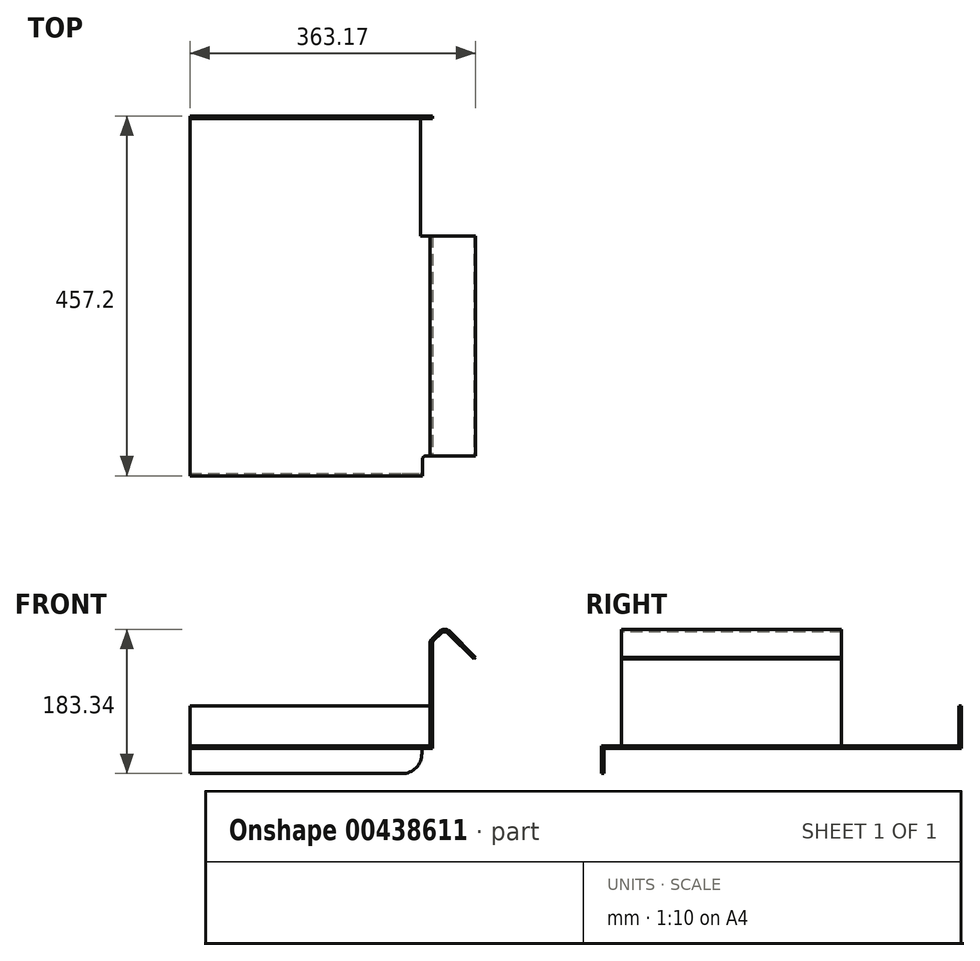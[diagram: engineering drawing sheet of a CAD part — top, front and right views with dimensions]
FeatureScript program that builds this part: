
annotation { "Feature Type Name" : "Feature", "Feature Type Description" : "" }
export const myFeature = defineFeature(function(context is Context, id is Id, definition is map)
    precondition{}
    {
        {
            var Q0;
            Q0=qCreatedBy(makeId("Front.planeOp"),FACE);
            var sketch = newSketch(context, id + "F0", { "sketchPlane" : qUnion([Q0])});
            skCircle(sketch, "E0", {"center": v(0, 0) * mm, "radius": 165.1 * mm});
            skSolve(sketch);
        }
        {
            var Q0;
            Q0=makeQuery(id+"F0.imprint","IMPRINT",FACE,{"disambiguationData":[TD([[makeQuery(id+"F0.imprint","IMPRINT",EDGE,{"derivedFrom":sQuery(id+"F0.wireOp",EDGE,"E0")}),1.0]])]});
            var sketch = newSketch(context, id + "F1", { "sketchPlane" : qUnion([Q0])});
            skLineSegment(sketch, "E1", {"start": v(-76.2, -184.15) * mm, "end": v(76.2, -184.15) * mm});
            skLineSegment(sketch, "E2", {"start": v(0, -184.15) * mm, "end": v(0, 0) * mm});
            skSolve(sketch);
        }
        {
            var Q0;
            Q0=qCreatedBy(makeId("Front.planeOp"),FACE);
            var sketch = newSketch(context, id + "F2", { "sketchPlane" : qUnion([Q0])});
            skLineSegment(sketch, "E3.bottom", {"start": v(-139.7, 0) * mm, "end": v(139.7, 0) * mm});
            skLineSegment(sketch, "E3.top", {"start": v(-139.7, -184.15) * mm, "end": v(139.7, -184.15) * mm});
            skLineSegment(sketch, "E3.left", {"start": v(-139.7, 0) * mm, "end": v(-139.7, -184.15) * mm});
            skLineSegment(sketch, "E3.right", {"start": v(139.7, 0) * mm, "end": v(139.7, -184.15) * mm});
            skLineSegment(sketch, "E4", {"start": v(139.7, -184.15) * mm, "end": v(313.98, -184.15) * mm, "construction": true});
            skSolve(sketch);
        }
        {
            var Q0;
            Q0=qCreatedBy(makeId("Front.planeOp"),FACE);
            var sketch = newSketch(context, id + "F3", { "sketchPlane" : qUnion([Q0])});
            skLineSegment(sketch, "E5", {"start": v(165.1, -184.15) * mm, "end": v(165.1, -54.75) * mm});
            skLineSegment(sketch, "E6", {"start": v(167.89, -48.01) * mm, "end": v(177.22, -38.68) * mm});
            skLineSegment(sketch, "E7", {"start": v(190.7, -38.68) * mm, "end": v(223.47, -71.45) * mm});
            skLineSegment(sketch, "E8", {"start": v(221.23, -73.7) * mm, "end": v(223.47, -71.45) * mm});
            skLineSegment(sketch, "E9", {"start": v(221.23, -73.7) * mm, "end": v(188.45, -40.92) * mm});
            skLineSegment(sketch, "E10", {"start": v(179.47, -40.92) * mm, "end": v(170.13, -50.26) * mm});
            skLineSegment(sketch, "E11", {"start": v(168.28, -54.75) * mm, "end": v(168.28, -184.15) * mm});
            skLineSegment(sketch, "E12", {"start": v(168.28, -184.15) * mm, "end": v(165.1, -184.15) * mm});
            skPoint(sketch, "E13.orphan", {"position": v(167.35, -53.05) * mm});
            skPoint(sketch, "E14.newPointB", {"position": v(168.28, -52.07) * mm});
            skArc(sketch, "E14.filletArc", {"start": v(170.13, -50.26) * mm, "mid": v(168.76, -52.32) * mm, "end": v(168.28, -54.75) * mm});
            skPoint(sketch, "E15.visualSharp", {"position": v(165.1, -50.8) * mm});
            skArc(sketch, "E15.filletArc", {"start": v(167.89, -48.01) * mm, "mid": v(165.83, -51.1) * mm, "end": v(165.1, -54.75) * mm});
            skPoint(sketch, "E16.visualSharp", {"position": v(183.96, -36.43) * mm});
            skArc(sketch, "E16.filletArc", {"start": v(188.45, -40.92) * mm, "mid": v(183.96, -39.06) * mm, "end": v(179.47, -40.92) * mm});
            skPoint(sketch, "E17.visualSharp", {"position": v(183.96, -31.94) * mm});
            skArc(sketch, "E17.filletArc", {"start": v(190.7, -38.68) * mm, "mid": v(183.96, -35.89) * mm, "end": v(177.22, -38.68) * mm});
            skSolve(sketch);
        }
        {
            var Q0;
            Q0=qCreatedBy(makeId("Front.planeOp"),FACE);
            var sketch = newSketch(context, id + "F4", { "sketchPlane" : qUnion([Q0])});
            skLineSegment(sketch, "E18.bottom", {"start": v(-139.7, -184.15) * mm, "end": v(168.28, -184.15) * mm});
            skLineSegment(sketch, "E18.top", {"start": v(-139.7, -187.33) * mm, "end": v(168.28, -187.33) * mm});
            skLineSegment(sketch, "E18.left", {"start": v(-139.7, -184.15) * mm, "end": v(-139.7, -187.33) * mm});
            skLineSegment(sketch, "E18.right", {"start": v(168.28, -184.15) * mm, "end": v(168.28, -187.33) * mm});
            skSolve(sketch);
        }
        {
            var Q0;
            Q0=qCreatedBy(makeId("Front.planeOp"),FACE);
            var sketch = newSketch(context, id + "F5", { "sketchPlane" : qUnion([Q0])});
            skLineSegment(sketch, "E19.bottom", {"start": v(-139.7, -187.33) * mm, "end": v(168.28, -187.33) * mm});
            skLineSegment(sketch, "E19.top", {"start": v(-139.7, -219.23) * mm, "end": v(155.02, -219.23) * mm});
            skLineSegment(sketch, "E19.left", {"start": v(-139.7, -187.33) * mm, "end": v(-139.7, -219.23) * mm});
            skLineSegment(sketch, "E19.right", {"start": v(155.02, -187.33) * mm, "end": v(155.02, -219.23) * mm});
            skSolve(sketch);
        }
        {
            var Q0;
            Q0 = qSketchRegion(id + "F4", true);
            extrude(context, id + "F6", {"entities" : qUnion([Q0]), "oppositeDirection" : true, "depth" : 457.2 * mm});
        }
        {
            var Q0;
            Q0 = qSketchRegion(id + "F5", true);
            extrude(context, id + "F7", {"entities" : qUnion([Q0]), "oppositeDirection" : true, "depth" : 3.17 * mm});
        }
        {
            var Q0;
            Q0=qCreatedBy(makeId("Right.planeOp"),FACE);
            var sketch = newSketch(context, id + "F8", { "sketchPlane" : qUnion([Q0])});
            skLineSegment(sketch, "E20.bottom", {"start": v(454.03, -133.35) * mm, "end": v(457.2, -133.35) * mm});
            skLineSegment(sketch, "E20.top", {"start": v(454.03, -184.15) * mm, "end": v(457.2, -184.15) * mm});
            skLineSegment(sketch, "E20.left", {"start": v(454.03, -133.35) * mm, "end": v(454.03, -184.15) * mm});
            skLineSegment(sketch, "E20.right", {"start": v(457.2, -133.35) * mm, "end": v(457.2, -184.15) * mm});
            skSolve(sketch);
        }
        {
            var Q0;
            Q0 = qSketchRegion(id + "F8", true);
            var Q1;
            Q1=makeQuery(id+"F6.opExtrude","SWEPT_FACE",FACE,{"disambiguationData":[OSD([sQuery(id+"F4.wireOp",EDGE,"E18.right")])]});
            var Q2;
            Q2=makeQuery(id+"F6.opExtrude","SWEPT_BODY",BODY,{"disambiguationData":[OSD([sQuery(id+"F4.wireOp",EDGE,"E18.bottom"),sQuery(id+"F4.wireOp",EDGE,"E18.top"),sQuery(id+"F4.wireOp",EDGE,"E18.left"),sQuery(id+"F4.wireOp",EDGE,"E18.right")])]});
            var Q3;
            Q3=makeQuery(id+"F6.opExtrude","SWEPT_BODY",BODY,{"disambiguationData":[OSD([sQuery(id+"F4.wireOp",EDGE,"E18.bottom"),sQuery(id+"F4.wireOp",EDGE,"E18.top"),sQuery(id+"F4.wireOp",EDGE,"E18.left"),sQuery(id+"F4.wireOp",EDGE,"E18.right")])]});
            extrude(context, id + "F9", {"entities" : qUnion([Q0]), "operationType" : NewBodyOperationType.ADD, "endBound" : BoundingType.UP_TO_SURFACE, "endBoundEntityFace" : qUnion([Q1]), "endBoundEntityBody" : qUnion([Q2]), "depth" : 139.7 * mm, "hasSecondDirection" : true, "secondDirectionOppositeDirection" : true, "secondDirectionBoundEntityBody" : qUnion([Q3]), "secondDirectionDepth" : 139.7 * mm});
        }
        {
            var Q0;
            Q0 = qSketchRegion(id + "F3", true);
            extrude(context, id + "F10", {"entities" : qUnion([Q0]), "oppositeDirection" : true, "depth" : 304.8 * mm});
        }
        {
            var Q0;
            Q0 = qSketchRegion(id + "F3", true);
            extrude(context, id + "F11", {"entities" : qUnion([Q0]), "operationType" : NewBodyOperationType.REMOVE, "oppositeDirection" : true, "depth" : 25.4 * mm});
        }
        {
            var Q0;
            Q0=makeQuery(id+"F6.opExtrude","SWEPT_FACE",FACE,{"disambiguationData":[OSD([sQuery(id+"F4.wireOp",EDGE,"E18.top")])]});
            var sketch = newSketch(context, id + "F12", { "sketchPlane" : qUnion([Q0])});
            skLineSegment(sketch, "E21", {"start": v(168.27, -454.03) * mm, "end": v(153.07, -454.03) * mm});
            skLineSegment(sketch, "E22", {"start": v(153.07, -454.03) * mm, "end": v(153.07, -304.8) * mm});
            skLineSegment(sketch, "E23", {"start": v(153.07, -304.8) * mm, "end": v(168.28, -304.8) * mm});
            skSolve(sketch);
        }
        {
            var Q0;
            {var subQ0=sQuery(id+"F12.wireOp",EDGE,"E21");Q0=makeQuery(id+"F12.imprint","IMPRINT",FACE,{"disambiguationData":[TD([[makeQuery(id+"F12.imprint","IMPRINT",EDGE,{"derivedFrom":subQ0}),-1.0]])]});}
            extrude(context, id + "F13", {"entities" : qUnion([Q0]), "operationType" : NewBodyOperationType.REMOVE, "oppositeDirection" : true, "depth" : 3.17 * mm});
        }
        {
            var Q0;
            Q0=qCreatedBy(makeId("Top.planeOp"),FACE);
            var sketch = newSketch(context, id + "F14", { "sketchPlane" : qUnion([Q0])});
            skLineSegment(sketch, "E24.bottom", {"start": v(168.28, 25.4) * mm, "end": v(155.58, 25.4) * mm});
            skLineSegment(sketch, "E24.top", {"start": v(168.28, 0) * mm, "end": v(155.58, 0) * mm});
            skLineSegment(sketch, "E24.left", {"start": v(168.28, 25.4) * mm, "end": v(168.28, 0) * mm});
            skLineSegment(sketch, "E24.right", {"start": v(155.58, 25.4) * mm, "end": v(155.58, 0) * mm});
            skSolve(sketch);
        }
        {
            var Q0;
            Q0 = qSketchRegion(id + "F14", true);
            extrude(context, id + "F15", {"entities" : qUnion([Q0]), "operationType" : NewBodyOperationType.REMOVE, "oppositeDirection" : true, "depth" : 304.8 * mm});
        }
        {
            var Q0;
            Q0=makeQuery(id+"F7.opExtrude","SWEPT_EDGE",EDGE,{"disambiguationData":[OSD([sQuery(id+"F5.wireOp",EDGE,"E19.top"),sQuery(id+"F5.wireOp",EDGE,"E19.right")])]});
            fillet(context, id + "F16", {"entities" : qUnion([Q0]), "radius" : 25.4 * mm, "tangentPropagation" : true, "allowEdgeOverflow" : false});
        }
        {
            var Q0;
            Q0=makeQuery(id+"F15.boolean.opBoolean","COPY",EDGE,{"derivedFrom":makeQuery(id+"F15.opExtrude","SWEPT_EDGE",EDGE,{"disambiguationData":[OSD([sQuery(id+"F14.wireOp",EDGE,"E24.bottom"),sQuery(id+"F14.wireOp",EDGE,"E24.right")])]})});
            fillet(context, id + "F17", {"entities" : qUnion([Q0]), "radius" : 5.08 * mm, "tangentPropagation" : true, "allowEdgeOverflow" : false});
        }
    });
